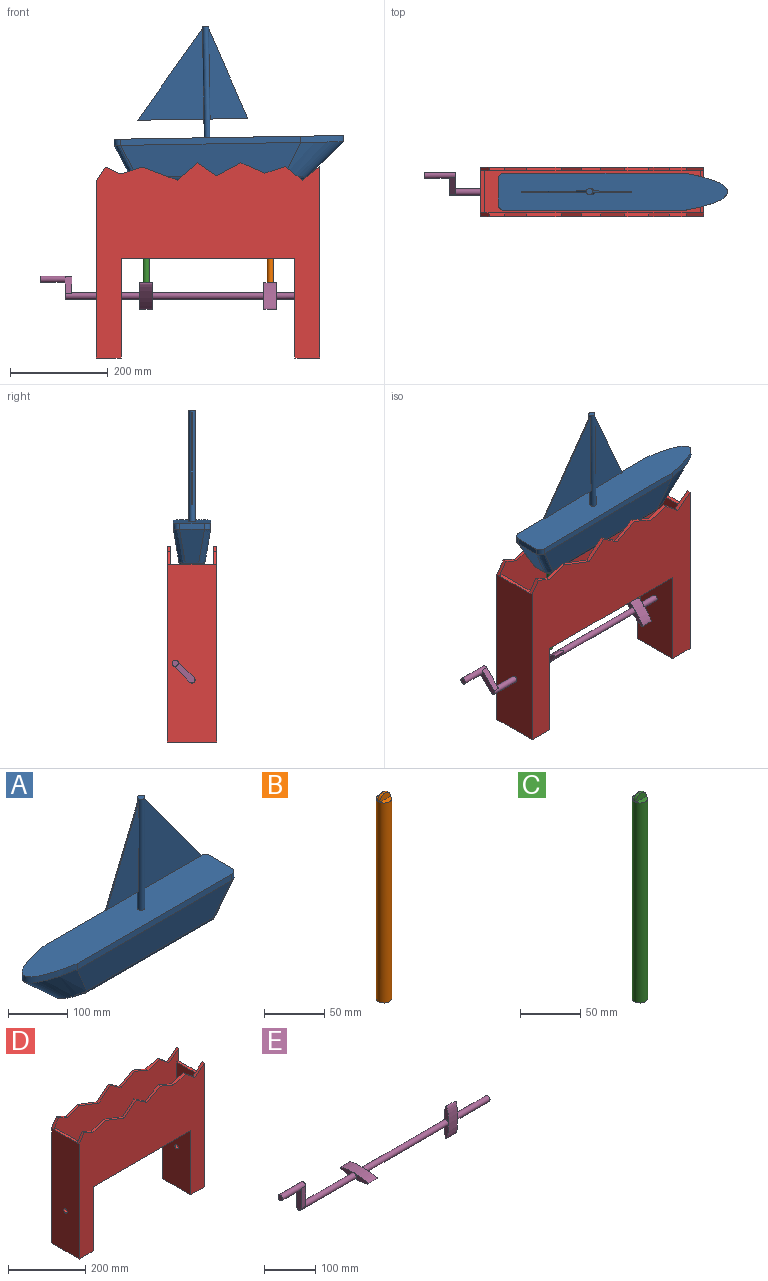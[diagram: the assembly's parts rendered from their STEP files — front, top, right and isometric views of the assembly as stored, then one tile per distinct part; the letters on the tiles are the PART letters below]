
ASSEMBLY  parts=5 mates=4
PART A: 41 faces, bbox 497.6x76.2x317.5 mm
  f0: cylinder r=6.35mm len=228.6mm, axis (0,0,-1), area 8172.9mm2, adj f14,f25,f27,f28,f29,f30,f31,f32
  f1: plane 335.26x29.29mm, normal (0,0,-1), area 9377.4mm2, adj f16,f17,f18,f19,f21,f22,f24,f38
  f2: bspline ~126.09x76.2mm, area 12187.8mm2, adj f3,f7,f10,f16,f18,f20,f22,f24
  f3: plane 368.3x65.59mm, normal (0,0.99,-0.16), area 22308.7mm2, adj f2,f4,f9,f24
  f4: bspline ~381x76.2mm, area 1483.6mm2, adj f3,f5,f8,f21,f23
  f5: plane 69.18x50.8mm, normal (0.89,0,-0.45), area 3037.3mm2, adj f4,f6,f13,f19
  f6: bspline ~381x76.2mm, area 1483.6mm2, adj f5,f7,f12,f15,f17
  f7: plane 368.3x65.59mm, normal (0,-0.99,-0.16), area 22308.7mm2, adj f2,f6,f11,f16
  f8: cylinder r=12.7mm len=12.7mm, axis (0,0,-1), area 253.4mm2, adj f4,f9,f13,f14
  f9: plane 368.3x12.7mm, normal (0,1,0), area 4677.4mm2, adj f3,f8,f10,f14
  f10: extruded ~87.99x76.2mm, area 2539.1mm2, adj f2,f9,f11,f14
  f11: plane 368.3x12.7mm, normal (0,-1,0), area 4677.4mm2, adj f7,f10,f12,f14
  f12: cylinder r=12.7mm len=12.7mm, axis (0,0,-1), area 253.4mm2, adj f6,f11,f13,f14
  f13: plane 50.8x12.7mm, normal (1,0,0), area 645.2mm2, adj f5,f8,f12,f14
  f14: plane 497.57x76.2mm, normal (0,0,1), area 33480.3mm2, adj f0,f8,f9,f10,f11,f12,f13
  f15: bspline ~12.53x10.61mm, area 94.5mm2, adj f6,f16,f17
  f16: cylinder r=12.7mm len=302.71mm, axis (1,0,0), area 5377.5mm2, adj f1,f2,f7,f15,f18
  f17: bspline ~11.67x8.29mm, area 66.9mm2, adj f1,f6,f15,f19
  f18: bspline ~44.61x27mm, area 629.8mm2, adj f1,f2,f16,f20
  f19: cylinder r=12.7mm len=27.74mm, axis (0,-1,0), area 390mm2, adj f1,f5,f17,f21
  f20: bspline ~13.07x9.02mm, area 48.9mm2, adj f2,f18,f22
  f21: bspline ~11.67x8.26mm, area 66mm2, adj f1,f4,f19,f23
  f22: bspline ~44.5x26.99mm, area 629.9mm2, adj f1,f2,f20,f24
  f23: bspline ~12.53x10.61mm, area 60.5mm2, adj f4,f21,f24
  f24: cylinder r=12.7mm len=302.71mm, axis (1,0,0), area 5377.5mm2, adj f1,f2,f3,f22,f23
  f25: plane 12.7x12.7mm, normal (0,0,1), area 126.7mm2, adj f0
  f26: plane 185.32x135.58mm, normal (0.81,0,0.59), area 583.2mm2, adj f27,f28,f29,f30,f31
  f27: plane 185.32x135.71mm, normal (0,1,0), area 12586.9mm2, adj f0,f26,f29,f31
  f28: plane 185.32x135.71mm, normal (0,-1,0), area 12586.9mm2, adj f0,f26,f29,f30
  f29: plane 135.71x2.54mm, normal (0,0,-1), area 344.5mm2, adj f0,f26,f27,f28
  f30: plane 1.27x0.13mm, normal (0,0,1), area 0.1mm2, adj f0,f26,f28
  f31: plane 1.27x0.13mm, normal (0,0,1), area 0.1mm2, adj f0,f26,f27
  f32: plane 1.27x0.13mm, normal (0,0,1), area 0.1mm2, adj f0,f35,f37
  f33: plane 77.17x2.54mm, normal (0,0,-1), area 195.8mm2, adj f0,f34,f35,f37
  f34: plane 185.32x77.17mm, normal (0,-1,0), area 7162.5mm2, adj f0,f33,f36,f37
  f35: plane 185.32x77.17mm, normal (0,1,0), area 7162.5mm2, adj f0,f32,f33,f37
  f36: plane 1.27x0.13mm, normal (0,0,1), area 0.1mm2, adj f0,f34,f37
  f37: plane 185.32x77.04mm, normal (-0.92,0,0.38), area 509.8mm2, adj f32,f33,f34,f35,f36
  f38: cylinder r=6.35mm len=7.62mm, axis (0,1,0), area 20.8mm2, adj f1,f39,f40
  f39: plane 7.62x1.27mm, normal (0,1,0), area 6.6mm2, adj f1,f38
  f40: plane 7.62x1.27mm, normal (0,-1,0), area 6.6mm2, adj f1,f38
PART B: 11 faces, bbox 12.7x12.7x209.6 mm
  f0: plane 12.44x5.08mm, normal (0,0,1), area 47.3mm2, adj f2,f9
  f1: plane 12.7x12.7mm, normal (0,0,-1), area 126.7mm2, adj f2
  f2: cylinder r=6.35mm len=203.2mm, axis (0,0,1), area 8107.3mm2, adj f0,f1,f3,f4,f5,f6,f7
  f3: plane 12.44x5.08mm, normal (0,0,1), area 47.3mm2, adj f2,f10
  f4: plane 1.27x0.13mm, normal (0,0,-1), area 0.1mm2, adj f2,f8,f10
  f5: plane 1.27x0.13mm, normal (0,0,-1), area 0.1mm2, adj f2,f8,f9
  f6: plane 1.27x0.13mm, normal (0,0,-1), area 0.1mm2, adj f2,f8,f10
  f7: plane 1.27x0.13mm, normal (0,0,-1), area 0.1mm2, adj f2,f8,f9
  f8: cylinder r=6.35mm len=12.7mm, axis (0,1,0), area 50.7mm2, adj f4,f5,f6,f7,f9,f10
  f9: plane 12.7x6.35mm, normal (0,-1,0), area 63.3mm2, adj f0,f5,f7,f8
  f10: plane 12.7x6.35mm, normal (0,1,0), area 63.3mm2, adj f3,f4,f6,f8
PART C: 11 faces, bbox 12.7x12.7x209.6 mm
  f0: plane 12.44x5.08mm, normal (0,0,1), area 47.3mm2, adj f3,f9
  f1: plane 12.7x12.7mm, normal (0,0,-1), area 126.7mm2, adj f3
  f2: plane 12.44x5.08mm, normal (0,0,1), area 47.3mm2, adj f3,f10
  f3: cylinder r=6.35mm len=203.2mm, axis (0,0,1), area 8107.3mm2, adj f0,f1,f2,f4,f5,f6,f7
  f4: plane 1.27x0.13mm, normal (0,0,-1), area 0.1mm2, adj f3,f8,f9
  f5: plane 1.27x0.13mm, normal (0,0,-1), area 0.1mm2, adj f3,f8,f10
  f6: plane 1.27x0.13mm, normal (0,0,-1), area 0.1mm2, adj f3,f8,f9
  f7: plane 1.27x0.13mm, normal (0,0,-1), area 0.1mm2, adj f3,f8,f10
  f8: cylinder r=6.35mm len=12.7mm, axis (0,1,0), area 50.7mm2, adj f4,f5,f6,f7,f9,f10
  f9: plane 12.7x6.35mm, normal (0,-1,0), area 63.3mm2, adj f0,f4,f6,f8
  f10: plane 12.7x6.35mm, normal (0,1,0), area 63.3mm2, adj f2,f5,f7,f8
PART D: 42 faces, bbox 457.2x101.6x399.3 mm
  f0: plane 457.2x145.33mm, normal (0,-1,0), area 57184.2mm2, adj f1,f5,f6,f16,f17,f18,f19,f20
  f1: plane 441.96x86.36mm, normal (0,0,1), area 37914.3mm2, adj f0,f2,f14,f15,f39,f41
  f2: plane 457.2x145.33mm, normal (0,1,0), area 57184.2mm2, adj f1,f5,f6,f27,f28,f29,f30,f31
  f3: plane 355.6x101.6mm, normal (0,0,-1), area 35875.6mm2, adj f8,f9,f10,f11,f14,f15
  f4: plane 101.6x50.8mm, normal (0,0,-1), area 5161.3mm2, adj f5,f9,f10,f11
  f5: plane 391.73x101.6mm, normal (1,0,0), area 36232.2mm2, adj f0,f2,f4,f10,f11,f12,f26,f37
  f6: plane 364x101.6mm, normal (-1,0,0), area 36795.5mm2, adj f0,f2,f7,f10,f11,f13,f16,f27
  f7: plane 101.6x50.8mm, normal (0,0,-1), area 5161.3mm2, adj f6,f8,f10,f11
  f8: plane 203.2x101.6mm, normal (1,0,0), area 20518.4mm2, adj f3,f7,f10,f11,f13
  f9: plane 203.2x101.6mm, normal (-1,0,0), area 20518.4mm2, adj f3,f4,f10,f11,f12
  f10: plane 457.2x399.33mm, normal (0,-1,0), area 102633.9mm2, adj f3,f4,f5,f6,f7,f8,f9,f27
  f11: plane 457.2x399.33mm, normal (0,1,0), area 102633.9mm2, adj f3,f4,f5,f6,f7,f8,f9,f16
  f12: cylinder r=6.35mm len=50.8mm, axis (-1,0,0), area 2026.8mm2, adj f5,f9
  f13: cylinder r=6.35mm len=50.8mm, axis (-1,0,0), area 2026.8mm2, adj f6,f8
  f14: cylinder r=6.35mm len=50.8mm, axis (0,0,1), area 2026.8mm2, adj f1,f3
  f15: cylinder r=6.35mm len=50.8mm, axis (0,0,1), area 2026.8mm2, adj f1,f3
  f16: plane 26.76x18.1mm, normal (-0.83,0,0.56), area 246.2mm2, adj f0,f6,f11,f17
  f17: plane 31.57x14.22mm, normal (0.41,0,0.91), area 263.9mm2, adj f0,f11,f16,f18
  f18: plane 45.39x14.22mm, normal (-0.3,0,0.95), area 362.5mm2, adj f0,f11,f17,f19
  f19: plane 70.07x26.76mm, normal (0.36,0,0.93), area 571.5mm2, adj f0,f11,f18,f20
  f20: plane 41.93x35.33mm, normal (-0.64,0,0.76), area 417.8mm2, adj f0,f11,f19,f21
  f21: plane 39.4x26.65mm, normal (0.56,0,0.83), area 362.4mm2, adj f0,f11,f20,f22
  f22: plane 49.32x26.65mm, normal (-0.48,0,0.88), area 427.2mm2, adj f0,f11,f21,f23
  f23: plane 49.04x20.83mm, normal (0.39,0,0.92), area 406mm2, adj f0,f11,f22,f24
  f24: plane 42.23x13.23mm, normal (-0.3,0,0.95), area 337.2mm2, adj f0,f11,f23,f25
  f25: plane 34.25x27.73mm, normal (0.63,0,0.78), area 335.8mm2, adj f0,f11,f24,f26
  f26: plane 35.91x27.73mm, normal (-0.61,0,0.79), area 345.7mm2, adj f0,f5,f11,f25
  f27: plane 26.76x18.1mm, normal (-0.83,0,0.56), area 246.2mm2, adj f2,f6,f10,f28
  f28: plane 31.57x14.22mm, normal (0.41,0,0.91), area 263.9mm2, adj f2,f10,f27,f29
  f29: plane 45.39x14.22mm, normal (-0.3,0,0.95), area 362.5mm2, adj f2,f10,f28,f30
  f30: plane 70.07x26.76mm, normal (0.36,0,0.93), area 571.5mm2, adj f2,f10,f29,f31
  f31: plane 41.93x35.33mm, normal (-0.64,0,0.76), area 417.8mm2, adj f2,f10,f30,f32
  f32: plane 39.4x26.65mm, normal (0.56,0,0.83), area 362.4mm2, adj f2,f10,f31,f33
  f33: plane 49.32x26.65mm, normal (-0.48,0,0.88), area 427.2mm2, adj f2,f10,f32,f34
  f34: plane 49.04x20.83mm, normal (0.39,0,0.92), area 406mm2, adj f2,f10,f33,f35
  f35: plane 42.23x13.23mm, normal (-0.3,0,0.95), area 337.2mm2, adj f2,f10,f34,f36
  f36: plane 34.25x27.73mm, normal (0.63,0,0.78), area 335.8mm2, adj f2,f10,f35,f37
  f37: plane 35.91x27.73mm, normal (-0.61,0,0.79), area 345.7mm2, adj f2,f5,f10,f36
  f38: plane 86.36x7.62mm, normal (0,0,1), area 658.1mm2, adj f0,f2,f5,f39
  f39: plane 97.89x86.36mm, normal (-1,0,0), area 8453.5mm2, adj f0,f1,f2,f38
  f40: plane 86.36x7.62mm, normal (0,0,1), area 658.1mm2, adj f0,f2,f6,f41
  f41: plane 109.3x86.36mm, normal (1,0,0), area 9439.4mm2, adj f0,f1,f2,f40
PART E: 20 faces, bbox 571.5x76.2x93 mm
  f0: cylinder r=6.35mm len=228.6mm, axis (-1,0,0), area 9120.7mm2, adj f5,f7,f10,f12
  f1: plane 12.7x12.7mm, normal (1,0,0), area 126.7mm2, adj f2
  f2: cylinder r=6.35mm len=88.9mm, axis (-1,0,0), area 3547mm2, adj f1,f4,f6
  f3: extruded ~76.2x25.4mm, area 4024.6mm2, adj f4,f5,f6,f7
  f4: plane 38.1x12.7mm, normal (1,0,0), area 316.7mm2, adj f2,f3
  f5: plane 38.1x12.7mm, normal (-1,0,0), area 316.7mm2, adj f0,f3
  f6: plane 38.1x12.7mm, normal (1,0,0), area 316.7mm2, adj f2,f3
  f7: plane 38.1x12.7mm, normal (-1,0,0), area 316.7mm2, adj f0,f3
  f8: extruded ~76.2x25.4mm, area 4024.6mm2, adj f9,f10,f11,f12
  f9: plane 38.1x12.7mm, normal (-1,0,0), area 316.7mm2, adj f8,f13
  f10: plane 38.1x12.7mm, normal (1,0,0), area 316.7mm2, adj f0,f8
  f11: plane 38.1x12.7mm, normal (-1,0,0), area 316.7mm2, adj f8,f13
  f12: plane 38.1x12.7mm, normal (1,0,0), area 316.7mm2, adj f0,f8
  f13: cylinder r=6.35mm len=152.4mm, axis (-1,0,0), area 5827.1mm2, adj f9,f11,f14,f15,f16,f17
  f14: plane 54.89x12.7mm, normal (1,0,0), area 616.4mm2, adj f13,f15,f16,f18
  f15: plane 48.54x12.7mm, normal (0,-1,0), area 616.4mm2, adj f13,f14,f17,f18
  f16: plane 48.54x12.7mm, normal (0,1,0), area 616.4mm2, adj f13,f14,f17,f18
  f17: plane 54.89x12.7mm, normal (-1,0,0), area 616.4mm2, adj f13,f15,f16,f18
  f18: cylinder r=6.35mm len=63.5mm, axis (1,0,0), area 2280.2mm2, adj f14,f15,f16,f17,f19
  f19: plane 12.7x12.7mm, normal (-1,0,0), area 126.7mm2, adj f18
PLACE A rot(axis=(-0.01,0,1),180deg) t=(11.78,59.67,33.44)mm
PLACE B t=(8.37,59.67,34.23)mm
PLACE C rot(axis=(-0.01,-0.01,1),0deg) t=(8.37,59.67,34.23)mm
PLACE D t=(8.37,59.67,6.92)mm fixed
PLACE E rot(axis=(-1,0,0),45deg) t=(8.37,59.67,6.92)mm
MATE slider C.f3 <-> D.f14  axis (0,0,1) through (-118.63,59.67,135.83)mm
MATE revolute E.f0 <-> D.f12  axis (1,0,0) through (236.97,59.67,6.92)mm
MATE revolute A.f40 <-> C.f9  axis (0,1,0) through (-118.63,58.4,240.12)mm
MATE slider B.f2 <-> D.f15  axis (0,0,1) through (135.37,59.67,135.83)mm
